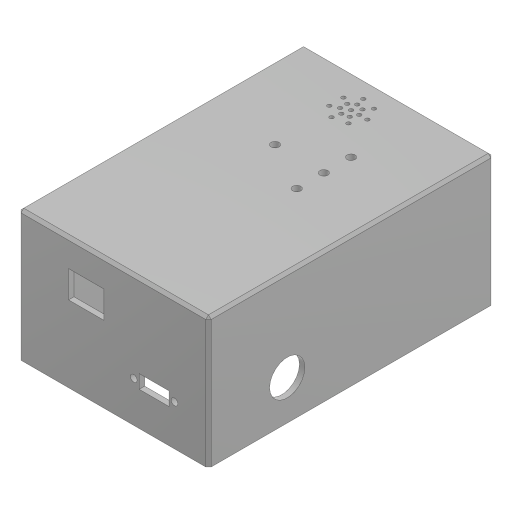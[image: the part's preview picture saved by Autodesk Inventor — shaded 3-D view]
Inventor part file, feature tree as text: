
AUTODESK INVENTOR PART (.ipt)
format: ipt  version: 2023.1 (Build 271208000, 208)  size: 314,368 bytes
history: native  units: mm
features: sketch x13, hole x8, extrude x6, chamfer x5, projected_geometry x2, shell x1, pattern_circular x1
ambient origin geometry x8: Origin, YZ Plane, XZ Plane, XY Plane, X Axis, Y Axis, Z Axis, Center Point
bodies: Volumenkörper1 (feature_tree)
feature tree (36):
  extrude  "Extrusion1"  Depth=70.0mm
  shell  "Wandung1"  Thickness=48.0mm
  extrude  "Extrusion12"  Depth=11.0mm
  chamfer  "Fase2"  Distance=3.0mm
  chamfer  "Fase3"  Distance=8.0mm
  chamfer  "Fase4"  Distance=5.0mm Angle=45.0deg
  chamfer  "Fase5"  Distance=5.0mm Angle=45.0deg
  hole  "Bohrung14"  [1 undecoded]
  chamfer  "Fase6"  Distance=62.0mm
  hole  "Button"  [1 undecoded]
  hole  "LEDS"  [1 undecoded]
  hole  "Sensor"  [1 undecoded]
  sketch  "Skizze20"  dims[d112=8.0mm d113=6.0mm d114=4.0mm d115=2.0mm d116=90.0deg d117=8.0mm d118=20.594885mm d149=11.0mm]
  extrude  "Extrusion9"  Depth=10.0mm
  hole  "Switch"  [1 undecoded]
  hole  "nRF-Antenna"  [1 undecoded]
  extrude  "PCB-holder"  Depth=23.5mm
  hole  "LED Green"  [1 undecoded]
  extrude  "Arduino Programming"  Depth=7.0mm
  extrude  "USB-C"  Depth=12.5mm
  hole  "Bohrung16"  [1 undecoded]
  pattern_circular  "Runde Anordnung3"  [2 undecoded]
  sketch  "Skizze1"  dims[d0=105.0mm d1=70.0mm d2=48.0mm d3=0.0mm]
  sketch  "Skizze11"  dims[d4=2.0mm]
  sketch  "Skizze12"  dims[d84=14.0mm d85=6.0mm d86=4.0mm d87=2.0mm d88=90.0deg d89=5.0mm d90=20.594885mm]
  sketch  "Skizze14"  dims[d95=3.0mm d96=6.0mm d97=4.0mm d98=2.0mm d99=90.0deg d100=8.0mm d101=20.594885mm]
  sketch  "Skizze22"  dims[d150=5.0mm]
  sketch  "Skizze25"  dims[d153=15.0mm d154=3.0mm d155=0.0mm]
  projected_geometry  "Projizierte Kontur5"
  sketch  "Skizze26"  dims[d156=2.5mm d157=6.0mm d158=4.0mm d159=2.0mm d160=90.0deg d161=8.0mm d162=20.594885mm]
  sketch  "Skizze27"  dims[d192=13.0mm d193=6.0mm d194=4.0mm d195=2.0mm d196=90.0deg d197=8.0mm d198=20.594885mm]
  sketch  "Skizze29"  dims[d208=5.0mm]
  sketch  "Skizze30"  dims[d209=5.0mm d210=8.0mm d211=0.0mm d212=5.0mm d213=2.0mm d214=45.0deg d215=5.0mm d216=2.0mm d217=45.0deg]
  projected_geometry  "Projizierte Kontur6"
  sketch  "Skizze31"  dims[d218=5.0mm d219=2.0mm d220=45.0deg d221=5.0mm d222=2.0mm d223=45.0deg]
  sketch  "Skizze32"  dims[d224=97.0mm d225=62.0mm d226=2.8mm d227=6.0mm d228=4.0mm d229=2.0mm d230=90.0deg d231=8.0mm d232=0.0mm d233=1.0mm d234=2.0mm d235=45.0deg d238=18.0mm d239=5.0mm d240=10.0mm d241=10.0mm d249=15.0mm d250=23.5mm d251=14.5mm d252=7.0mm d253=87.0mm d254=52.0mm d255=2.8mm d256=10.0mm d257=0.0mm d258=10.0mm d259=15.0mm d260=29.0mm d268=10.0mm d269=8.0mm d271=3.0mm d272=6.0mm d273=4.0mm d274=2.0mm d275=90.0deg d276=8.0mm d277=20.594885mm d278=15.0mm d279=15.0mm d280=11.0mm d282=10.0mm d283=10.0mm d284=0.0mm d285=15.0mm d286=12.0mm d287=20.0mm d288=20.0mm d289=10.0mm d290=33.0mm d291=13.0mm d292=10.0mm d293=10.0mm d294=0.0mm d295=3.0mm d296=3.0mm d297=40.0mm d298=5.0mm d299=1.5mm d300=6.0mm d301=4.0mm d302=2.0mm d303=90.0deg d304=8.0mm d305=20.594885mm d306=70.0mm d307=360.0deg d309=12.5mm]
note: 10 required parameter values undecoded (feature->parameter linkage not recoverable at this tier; creation-order binding heuristic only, values carry confidence <= 0.55)
